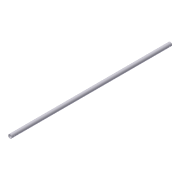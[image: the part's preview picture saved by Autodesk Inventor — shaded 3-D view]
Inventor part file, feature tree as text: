
AUTODESK INVENTOR PART (.ipt)
format: ipt  version: 2012 (Build 160160000, 160)  size: 84,992 bytes
history: native  units: in
note: dims shown in document units (in); Inventor stores cm internally (conversion verified against a paired STEP export)
features: extrude x2, plane x2, sketch x2, pattern_linear x1, mirror x1, other x1, projected_geometry x1
ambient origin geometry x8: Origin, YZ Plane, XZ Plane, XY Plane, X Axis, Y Axis, Z Axis, Center Point
bodies: Solid1 (feature_tree)
feature tree (10):
  extrude  "Extrusion1"  Depth=1.375in
  plane  "Work Plane1"
  extrude  "Extrusion2"  TaperAngle=0.0deg  [1 undecoded]
  pattern_linear  "Rectangular Pattern1"  Spacing1=0.25in  [1 undecoded]
  plane  "Work Plane2"
  mirror  "Mirror1"
  sketch  "Sketch1"  dims[d0=1.656in d1=1.375in]
  other  "Work Axis1"
  sketch  "Sketch2"  dims[d2=72.0in d3=0.0in d4=0.0in d5=0.25in d6=1.25in d7=15.0in d8=0.0in d9=0.7874in d11=2.0in]
  projected_geometry  "Projected Loop1"
note: 2 required parameter values undecoded (feature->parameter linkage not recoverable at this tier; creation-order binding heuristic only, values carry confidence <= 0.55)
